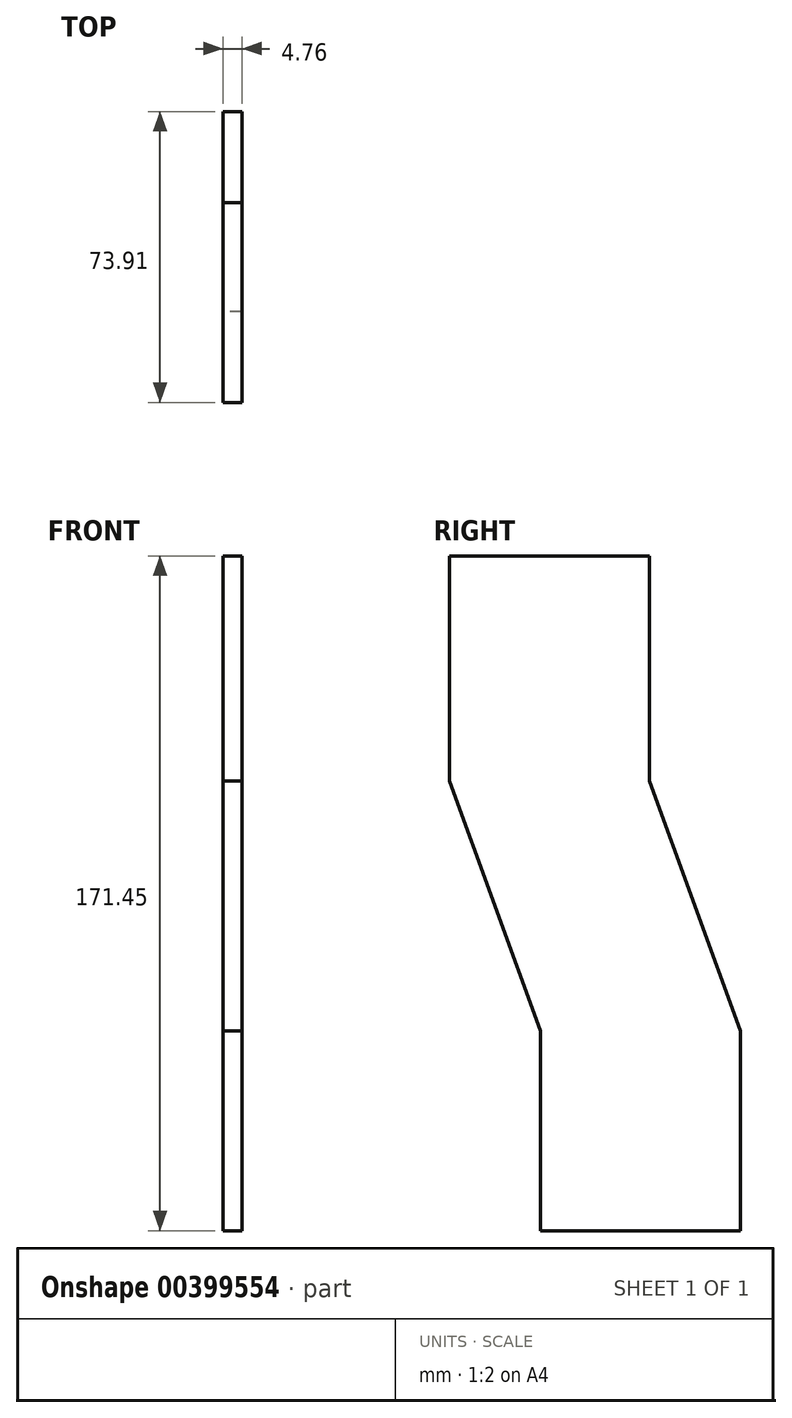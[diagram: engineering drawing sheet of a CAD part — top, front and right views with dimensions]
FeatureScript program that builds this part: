
annotation { "Feature Type Name" : "Feature", "Feature Type Description" : "" }
export const myFeature = defineFeature(function(context is Context, id is Id, definition is map)
    precondition{}
    {
        {
            var Q0;
            Q0=qCreatedBy(makeId("Right.planeOp"),FACE);
            var sketch = newSketch(context, id + "F0", { "sketchPlane" : qUnion([Q0])});
            skLineSegment(sketch, "E0.right", {"start": v(-25.4, 50.8) * mm, "end": v(-25.4, 0) * mm});
            skLineSegment(sketch, "E1", {"start": v(-25.4, 50.8) * mm, "end": v(-48.51, 114.3) * mm});
            skLineSegment(sketch, "E2", {"start": v(-48.51, 114.3) * mm, "end": v(-48.51, 171.45) * mm});
            skLineSegment(sketch, "E3", {"start": v(-48.51, 171.45) * mm, "end": v(2.29, 171.45) * mm});
            skLineSegment(sketch, "E4", {"start": v(2.29, 171.45) * mm, "end": v(2.29, 114.3) * mm});
            skLineSegment(sketch, "E5", {"start": v(2.29, 114.3) * mm, "end": v(25.4, 50.8) * mm});
            skLineSegment(sketch, "E6", {"start": v(-25.4, 0) * mm, "end": v(25.4, 0) * mm});
            skLineSegment(sketch, "E7", {"start": v(25.4, 0) * mm, "end": v(25.4, 50.8) * mm});
            skSolve(sketch);
        }
        {
            var Q0;
            Q0=makeQuery(id+"F0.imprint","IMPRINT",FACE,{"disambiguationData":[TD([[makeQuery(id+"F0.imprint","IMPRINT",EDGE,{"derivedFrom":sQuery(id+"F0.wireOp",EDGE,"E0.bottom")}),1.0]])]});
            var Q1;
            Q1=makeQuery(id+"F0.imprint","IMPRINT",FACE,{"disambiguationData":[TD([[makeQuery(id+"F0.imprint","IMPRINT",EDGE,{"derivedFrom":sQuery(id+"F0.wireOp",EDGE,"E0.right")}),1.0]])]});
            extrude(context, id + "F1", {"entities" : qUnion([Q0, Q1]), "depth" : 4.76 * mm});
        }
    });
